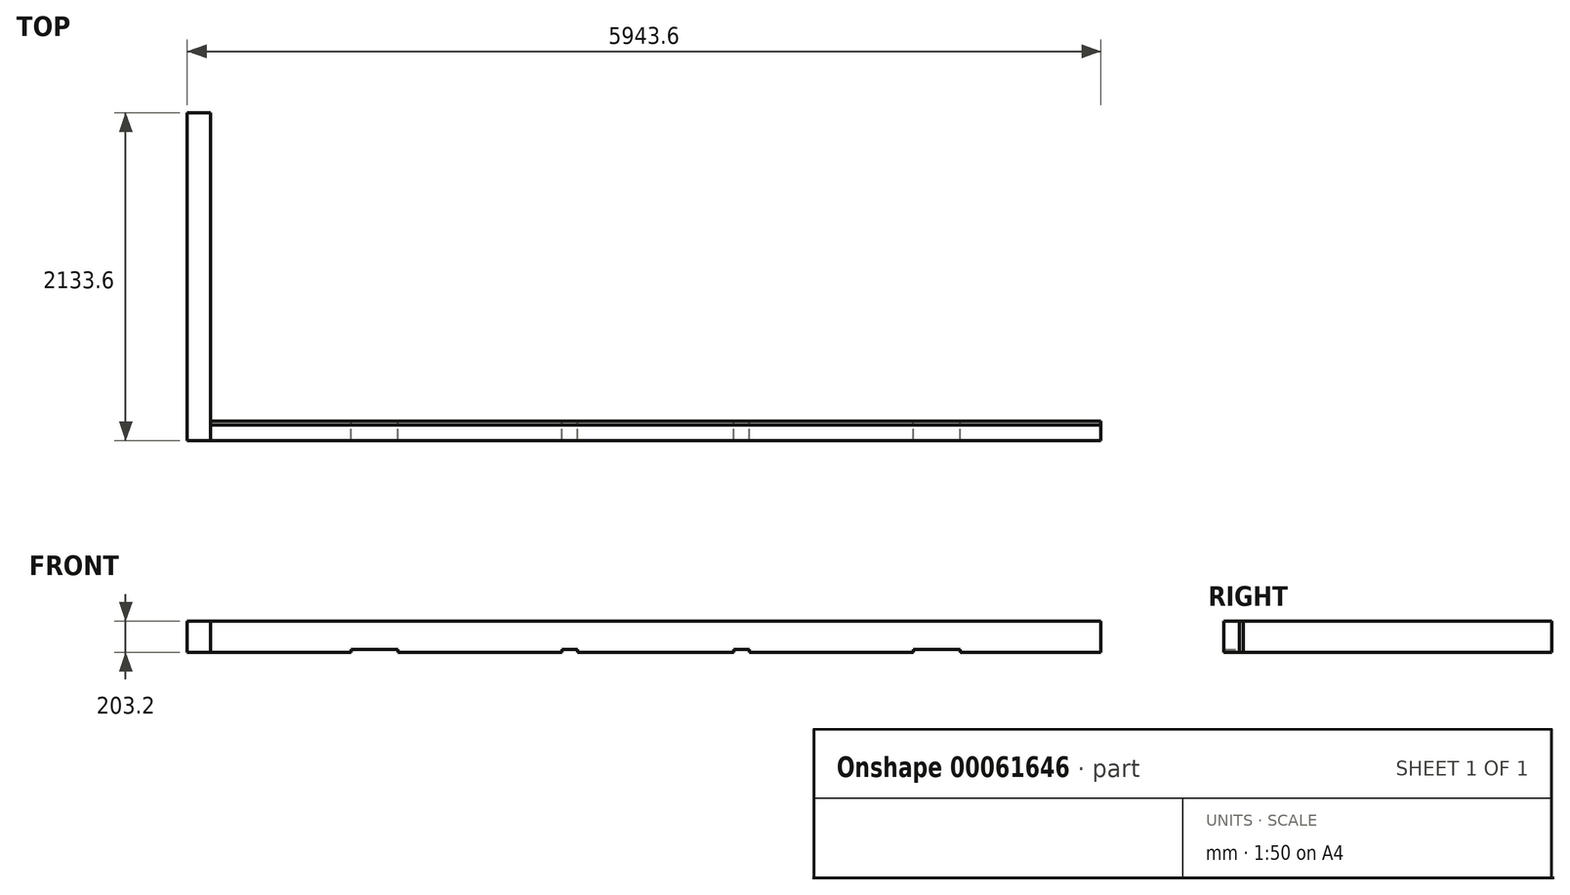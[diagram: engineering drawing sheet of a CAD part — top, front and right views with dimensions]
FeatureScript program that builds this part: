
annotation { "Feature Type Name" : "Feature", "Feature Type Description" : "" }
export const myFeature = defineFeature(function(context is Context, id is Id, definition is map)
    precondition{}
    {
        {
            var Q0;
            Q0=qCreatedBy(makeId("Top.planeOp"),FACE);
            var sketch = newSketch(context, id + "F0", { "sketchPlane" : qUnion([Q0])});
            skLineSegment(sketch, "E0.bottom", {"start": v(0, 0) * mm, "end": v(5791.2, 0) * mm});
            skLineSegment(sketch, "E0.top", {"start": v(0, 127) * mm, "end": v(5791.2, 127) * mm});
            skLineSegment(sketch, "E0.left", {"start": v(0, 0) * mm, "end": v(0, 127) * mm});
            skLineSegment(sketch, "E0.right", {"start": v(5791.2, 0) * mm, "end": v(5791.2, 127) * mm});
            skLineSegment(sketch, "E1", {"start": v(2895.6, 127) * mm, "end": v(2895.6, -244.32) * mm, "construction": true});
            skPoint(sketch, "E1.endSnap0", {"position": v(2895.6, 0) * mm});
            skSolve(sketch);
        }
        {
            var Q0;
            Q0=makeQuery(id+"F0.imprint","IMPRINT",FACE,{"disambiguationData":[TD([[makeQuery(id+"F0.imprint","IMPRINT",EDGE,{"derivedFrom":sQuery(id+"F0.wireOp",EDGE,"E0.bottom")}),1.0]])]});
            extrude(context, id + "F1", {"entities" : qUnion([Q0]), "depth" : 203.2 * mm});
        }
        {
            var Q0;
            Q0=makeQuery(id+"F1.opExtrude","CAP_FACE",FACE,{"disambiguationData":[OSD([sQuery(id+"F0.wireOp",EDGE,"E0.bottom"),sQuery(id+"F0.wireOp",EDGE,"E0.top"),sQuery(id+"F0.wireOp",EDGE,"E0.left"),sQuery(id+"F0.wireOp",EDGE,"E0.right")])],"isStart":true});
            var sketch = newSketch(context, id + "F2", { "sketchPlane" : qUnion([Q0])});
            skLineSegment(sketch, "E2", {"start": v(2895.6, -127) * mm, "end": v(2895.6, 0) * mm, "construction": true});
            skLineSegment(sketch, "E3.bottom", {"start": v(914.4, 0) * mm, "end": v(1219.2, 0) * mm});
            skLineSegment(sketch, "E3.top", {"start": v(914.4, -127) * mm, "end": v(1219.2, -127) * mm});
            skLineSegment(sketch, "E3.left", {"start": v(914.4, 0) * mm, "end": v(914.4, -127) * mm});
            skLineSegment(sketch, "E3.right", {"start": v(1219.2, 0) * mm, "end": v(1219.2, -127) * mm});
            skLineSegment(sketch, "E4.bottom", {"start": v(2387.6, 0) * mm, "end": v(2286, 0) * mm});
            skLineSegment(sketch, "E4.top", {"start": v(2387.6, -127) * mm, "end": v(2286, -127) * mm});
            skLineSegment(sketch, "E4.left", {"start": v(2387.6, 0) * mm, "end": v(2387.6, -127) * mm});
            skLineSegment(sketch, "E4.right", {"start": v(2286, 0) * mm, "end": v(2286, -127) * mm});
            skLineSegment(sketch, "E5.MirrorCS", {"start": v(3403.6, -127) * mm, "end": v(3505.2, -127) * mm});
            skLineSegment(sketch, "E6.MirrorCS", {"start": v(3505.2, 0) * mm, "end": v(3505.2, -127) * mm});
            skLineSegment(sketch, "E7.MirrorCS", {"start": v(3403.6, 0) * mm, "end": v(3505.2, 0) * mm});
            skLineSegment(sketch, "E8.MirrorCS", {"start": v(3403.6, 0) * mm, "end": v(3403.6, -127) * mm});
            skLineSegment(sketch, "E9.MirrorCS", {"start": v(4572, 0) * mm, "end": v(4572, -127) * mm});
            skLineSegment(sketch, "E10.MirrorCS", {"start": v(4876.8, 0) * mm, "end": v(4876.8, -127) * mm});
            skLineSegment(sketch, "E11.MirrorCS", {"start": v(4876.8, -127) * mm, "end": v(4572, -127) * mm});
            skLineSegment(sketch, "E12.MirrorCS", {"start": v(4876.8, 0) * mm, "end": v(4572, 0) * mm});
            skSolve(sketch);
        }
        {
            var Q0;
            Q0 = qSketchRegion(id + "F2", true);
            extrude(context, id + "F3", {"entities" : qUnion([Q0]), "operationType" : NewBodyOperationType.REMOVE, "oppositeDirection" : true, "depth" : 19.05 * mm});
        }
        {
            var Q0;
            Q0=qCreatedBy(makeId("Top.planeOp"),FACE);
            var sketch = newSketch(context, id + "F4", { "sketchPlane" : qUnion([Q0])});
            skLineSegment(sketch, "E13.bottom", {"start": v(0, 0) * mm, "end": v(5791.2, 0) * mm});
            skLineSegment(sketch, "E13.top", {"start": v(0, 101.6) * mm, "end": v(5791.2, 101.6) * mm});
            skLineSegment(sketch, "E13.left", {"start": v(0, 0) * mm, "end": v(0, 101.6) * mm});
            skLineSegment(sketch, "E13.right", {"start": v(5791.2, 0) * mm, "end": v(5791.2, 101.6) * mm});
            skSolve(sketch);
        }
        {
            var Q0;
            Q0 = qSketchRegion(id + "F4", true);
            extrude(context, id + "F5", {"entities" : qUnion([Q0]), "depth" : 203.2 * mm});
        }
        {
            var Q0;
            Q0 = qSketchRegion(id + "F2", true);
            extrude(context, id + "F6", {"entities" : qUnion([Q0]), "operationType" : NewBodyOperationType.REMOVE, "oppositeDirection" : true, "depth" : 19.05 * mm});
        }
        {
            var Q0;
            Q0=qCreatedBy(makeId("Top.planeOp"),FACE);
            var sketch = newSketch(context, id + "F7", { "sketchPlane" : qUnion([Q0])});
            skLineSegment(sketch, "E14.bottom", {"start": v(0, 0) * mm, "end": v(-152.4, 0) * mm});
            skLineSegment(sketch, "E14.top", {"start": v(0, 2133.6) * mm, "end": v(-152.4, 2133.6) * mm});
            skLineSegment(sketch, "E14.left", {"start": v(0, 0) * mm, "end": v(0, 2133.6) * mm});
            skLineSegment(sketch, "E14.right", {"start": v(-152.4, 0) * mm, "end": v(-152.4, 2133.6) * mm});
            skSolve(sketch);
        }
        {
            var Q0;
            Q0 = qSketchRegion(id + "F7", true);
            extrude(context, id + "F8", {"entities" : qUnion([Q0]), "depth" : 203.2 * mm});
        }
    });
